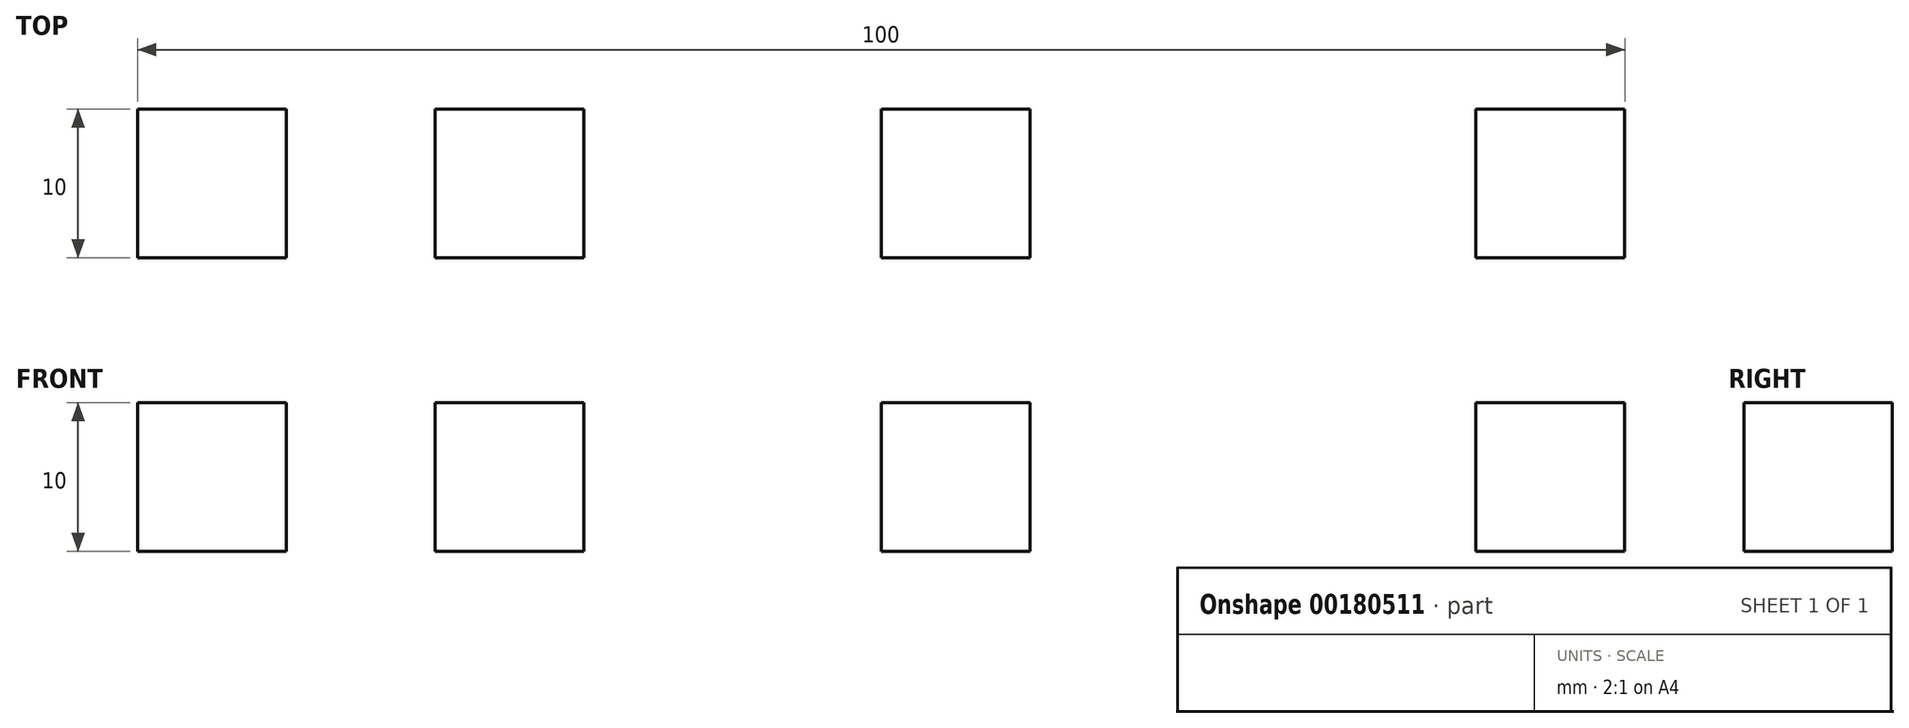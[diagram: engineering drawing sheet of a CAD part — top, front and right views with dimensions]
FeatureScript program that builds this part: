
annotation { "Feature Type Name" : "Feature", "Feature Type Description" : "" }
export const myFeature = defineFeature(function(context is Context, id is Id, definition is map)
    precondition{}
    {
        {
            var Q0;
            Q0=qCreatedBy(makeId("Top.planeOp"),FACE);
            var sketch = newSketch(context, id + "F0", { "sketchPlane" : qUnion([Q0])});
            skLineSegment(sketch, "E0.bottom", {"start": v(-77.23, 11.18) * mm, "end": v(-67.23, 11.18) * mm});
            skLineSegment(sketch, "E0.top", {"start": v(-77.23, 1.18) * mm, "end": v(-67.23, 1.18) * mm});
            skLineSegment(sketch, "E0.left", {"start": v(-77.23, 11.18) * mm, "end": v(-77.23, 1.18) * mm});
            skLineSegment(sketch, "E0.right", {"start": v(-67.23, 11.18) * mm, "end": v(-67.23, 1.18) * mm});
            skLineSegment(sketch, "E1.bottom", {"start": v(-57.23, 11.18) * mm, "end": v(-47.23, 11.18) * mm});
            skLineSegment(sketch, "E1.top", {"start": v(-57.23, 1.18) * mm, "end": v(-47.23, 1.18) * mm});
            skLineSegment(sketch, "E1.left", {"start": v(-57.23, 11.18) * mm, "end": v(-57.23, 1.18) * mm});
            skLineSegment(sketch, "E1.right", {"start": v(-47.23, 11.18) * mm, "end": v(-47.23, 1.18) * mm});
            skLineSegment(sketch, "E2.bottom", {"start": v(-27.23, 11.18) * mm, "end": v(-17.23, 11.18) * mm});
            skLineSegment(sketch, "E2.top", {"start": v(-27.23, 1.18) * mm, "end": v(-17.23, 1.18) * mm});
            skLineSegment(sketch, "E2.left", {"start": v(-27.23, 11.18) * mm, "end": v(-27.23, 1.18) * mm});
            skLineSegment(sketch, "E2.right", {"start": v(-17.23, 11.18) * mm, "end": v(-17.23, 1.18) * mm});
            skLineSegment(sketch, "E3.bottom", {"start": v(12.77, 11.18) * mm, "end": v(22.77, 11.18) * mm});
            skLineSegment(sketch, "E3.top", {"start": v(12.77, 1.18) * mm, "end": v(22.77, 1.18) * mm});
            skLineSegment(sketch, "E3.left", {"start": v(12.77, 11.18) * mm, "end": v(12.77, 1.18) * mm});
            skLineSegment(sketch, "E3.right", {"start": v(22.77, 11.18) * mm, "end": v(22.77, 1.18) * mm});
            skSolve(sketch);
        }
        {
            var Q0;
            Q0=makeQuery(id+"F0.imprint","IMPRINT",FACE,{"disambiguationData":[TD([[makeQuery(id+"F0.imprint","IMPRINT",EDGE,{"derivedFrom":sQuery(id+"F0.wireOp",EDGE,"E0.bottom")}),-1.0]])]});
            var Q1;
            Q1=makeQuery(id+"F0.imprint","IMPRINT",FACE,{"disambiguationData":[TD([[makeQuery(id+"F0.imprint","IMPRINT",EDGE,{"derivedFrom":sQuery(id+"F0.wireOp",EDGE,"E1.bottom")}),-1.0]])]});
            var Q2;
            Q2=makeQuery(id+"F0.imprint","IMPRINT",FACE,{"disambiguationData":[TD([[makeQuery(id+"F0.imprint","IMPRINT",EDGE,{"derivedFrom":sQuery(id+"F0.wireOp",EDGE,"E2.bottom")}),-1.0]])]});
            var Q3;
            Q3=makeQuery(id+"F0.imprint","IMPRINT",FACE,{"disambiguationData":[TD([[makeQuery(id+"F0.imprint","IMPRINT",EDGE,{"derivedFrom":sQuery(id+"F0.wireOp",EDGE,"E3.bottom")}),-1.0]])]});
            extrude(context, id + "F1", {"entities" : qUnion([Q0, Q1, Q2, Q3]), "depth" : 10 * mm});
        }
    });
